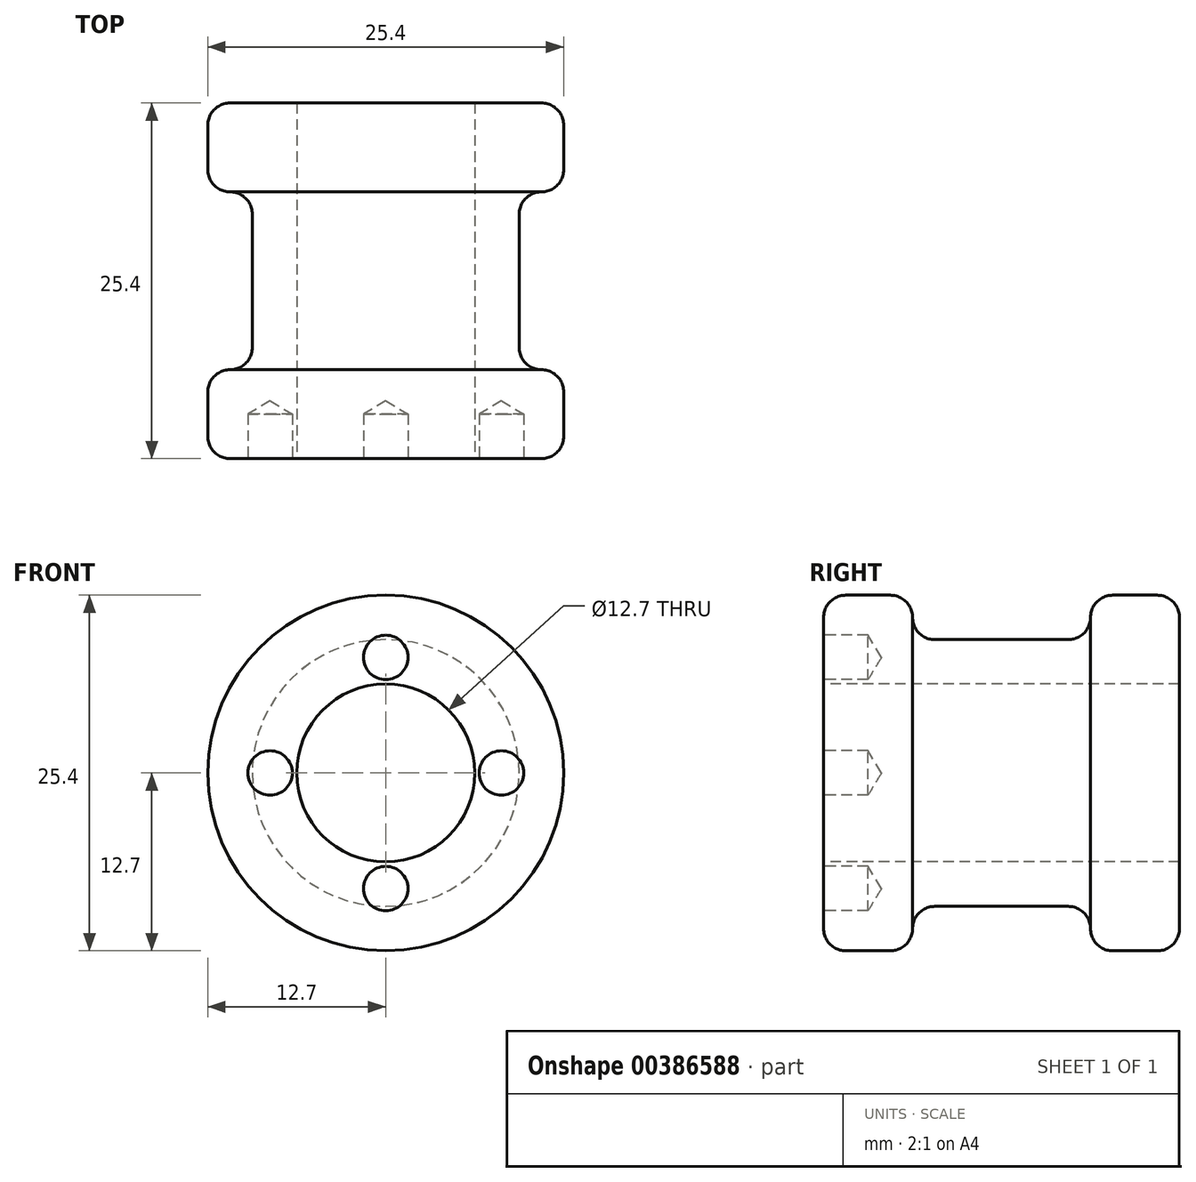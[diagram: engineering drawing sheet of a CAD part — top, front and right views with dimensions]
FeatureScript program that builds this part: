
annotation { "Feature Type Name" : "Feature", "Feature Type Description" : "" }
export const myFeature = defineFeature(function(context is Context, id is Id, definition is map)
    precondition{}
    {
        {
            var Q0;
            Q0=qCreatedBy(makeId("Front.planeOp"),FACE);
            var sketch = newSketch(context, id + "F0", { "sketchPlane" : qUnion([Q0])});
            skCircle(sketch, "E0", {"center": v(0, 0) * mm, "radius": 12.7 * mm});
            skSolve(sketch);
        }
        {
            var Q0;
            Q0 = qSketchRegion(id + "F0", true);
            extrude(context, id + "F1", {"entities" : qUnion([Q0]), "depth" : 6.35 * mm});
        }
        {
            var Q0;
            Q0=makeQuery(id+"F1.opExtrude","CAP_FACE",FACE,{"disambiguationData":[OSD([sQuery(id+"F0.wireOp",EDGE,"E0")])],"isStart":true});
            var sketch = newSketch(context, id + "F2", { "sketchPlane" : qUnion([Q0])});
            skCircle(sketch, "E1", {"center": v(0, 0) * mm, "radius": 9.53 * mm});
            skSolve(sketch);
        }
        {
            var Q0;
            Q0 = qSketchRegion(id + "F2", true);
            extrude(context, id + "F3", {"entities" : qUnion([Q0]), "operationType" : NewBodyOperationType.ADD, "depth" : 12.7 * mm});
        }
        {
            var Q0;
            Q0=makeQuery(id+"F3.opExtrude","CAP_FACE",FACE,{"disambiguationData":[OSD([sQuery(id+"F2.wireOp",EDGE,"E1")])],"isStart":false});
            var sketch = newSketch(context, id + "F4", { "sketchPlane" : qUnion([Q0])});
            skCircle(sketch, "E2", {"center": v(0, 0) * mm, "radius": 12.7 * mm});
            skSolve(sketch);
        }
        {
            var Q0;
            Q0 = qSketchRegion(id + "F4", true);
            extrude(context, id + "F5", {"entities" : qUnion([Q0]), "operationType" : NewBodyOperationType.ADD, "depth" : 6.35 * mm});
        }
        {
            var Q0;
            Q0=makeQuery(id+"F1.opExtrude","CAP_FACE",FACE,{"disambiguationData":[OSD([sQuery(id+"F0.wireOp",EDGE,"E0")])],"isStart":false});
            var sketch = newSketch(context, id + "F6", { "sketchPlane" : qUnion([Q0])});
            skPoint(sketch, "E3", {"position": v(0, 0) * mm});
            skSolve(sketch);
        }
        {
            var Q0;
            Q0=sQuery(id+"F6.wireOp",VERTEX,"E3");
            var Q1;
            Q1=makeQuery(id+"F1.opExtrude","SWEPT_BODY",BODY,{"disambiguationData":[OSD([sQuery(id+"F0.wireOp",EDGE,"E0")])]});
            hole(context, id + "F7", {"style" : HoleStyle.SIMPLE, "endStyle" : HoleEndStyle.THROUGH, "holeDiameter" : 12.7 * mm, "isTappedThrough" : true, "tappedDepth" : 12.7 * mm, "tapClearance" : 3, "locations" : qUnion([Q0]), "scope" : qUnion([Q1])});
        }
        {
            var Q0;
            Q0=makeQuery(id+"F1.opExtrude","CAP_FACE",FACE,{"disambiguationData":[OSD([sQuery(id+"F0.wireOp",EDGE,"E0")])],"isStart":false});
            var sketch = newSketch(context, id + "F8", { "sketchPlane" : qUnion([Q0])});
            skPoint(sketch, "E4", {"position": v(0, 8.26) * mm});
            skPoint(sketch, "E5", {"position": v(8.26, 0) * mm});
            skPoint(sketch, "E6", {"position": v(0, -8.26) * mm});
            skPoint(sketch, "E7", {"position": v(-8.26, 0) * mm});
            skSolve(sketch);
        }
        {
            var Q0;
            Q0=sQuery(id+"F8.wireOp",VERTEX,"E4");
            var Q1;
            Q1=sQuery(id+"F8.wireOp",VERTEX,"E7");
            var Q2;
            Q2=sQuery(id+"F8.wireOp",VERTEX,"E5");
            var Q3;
            Q3=sQuery(id+"F8.wireOp",VERTEX,"E6");
            var Q4;
            Q4=makeQuery(id+"F1.opExtrude","SWEPT_BODY",BODY,{"disambiguationData":[OSD([sQuery(id+"F0.wireOp",EDGE,"E0")])]});
            hole(context, id + "F9", {"style" : HoleStyle.SIMPLE, "endStyle" : HoleEndStyle.BLIND, "holeDiameter" : 3.17 * mm, "holeDepth" : 3.17 * mm, "isTappedThrough" : true, "tappedDepth" : 12.7 * mm, "tapClearance" : 3, "locations" : qUnion([Q0, Q1, Q2, Q3]), "scope" : qUnion([Q4])});
        }
        {
            var Q0;
            Q0=makeQuery(id+"F5.opExtrude","CAP_FACE",FACE,{"disambiguationData":[OSD([sQuery(id+"F4.wireOp",EDGE,"E2")])],"isStart":true});
            var Q1;
            Q1=makeQuery(id+"F1.opExtrude","CAP_FACE",FACE,{"disambiguationData":[OSD([sQuery(id+"F0.wireOp",EDGE,"E0")])],"isStart":true});
            var Q2;
            Q2=makeQuery(id+"F5.opExtrude","CAP_EDGE",EDGE,{"disambiguationData":[OSD([sQuery(id+"F4.wireOp",EDGE,"E2")])],"isStart":false});
            var Q3;
            Q3=makeQuery(id+"F1.opExtrude","CAP_EDGE",EDGE,{"disambiguationData":[OSD([sQuery(id+"F0.wireOp",EDGE,"E0")])],"isStart":false});
            fillet(context, id + "F10", {"entities" : qUnion([Q0, Q1, Q2, Q3]), "radius" : 1.59 * mm, "tangentPropagation" : true, "allowEdgeOverflow" : false});
        }
    });
